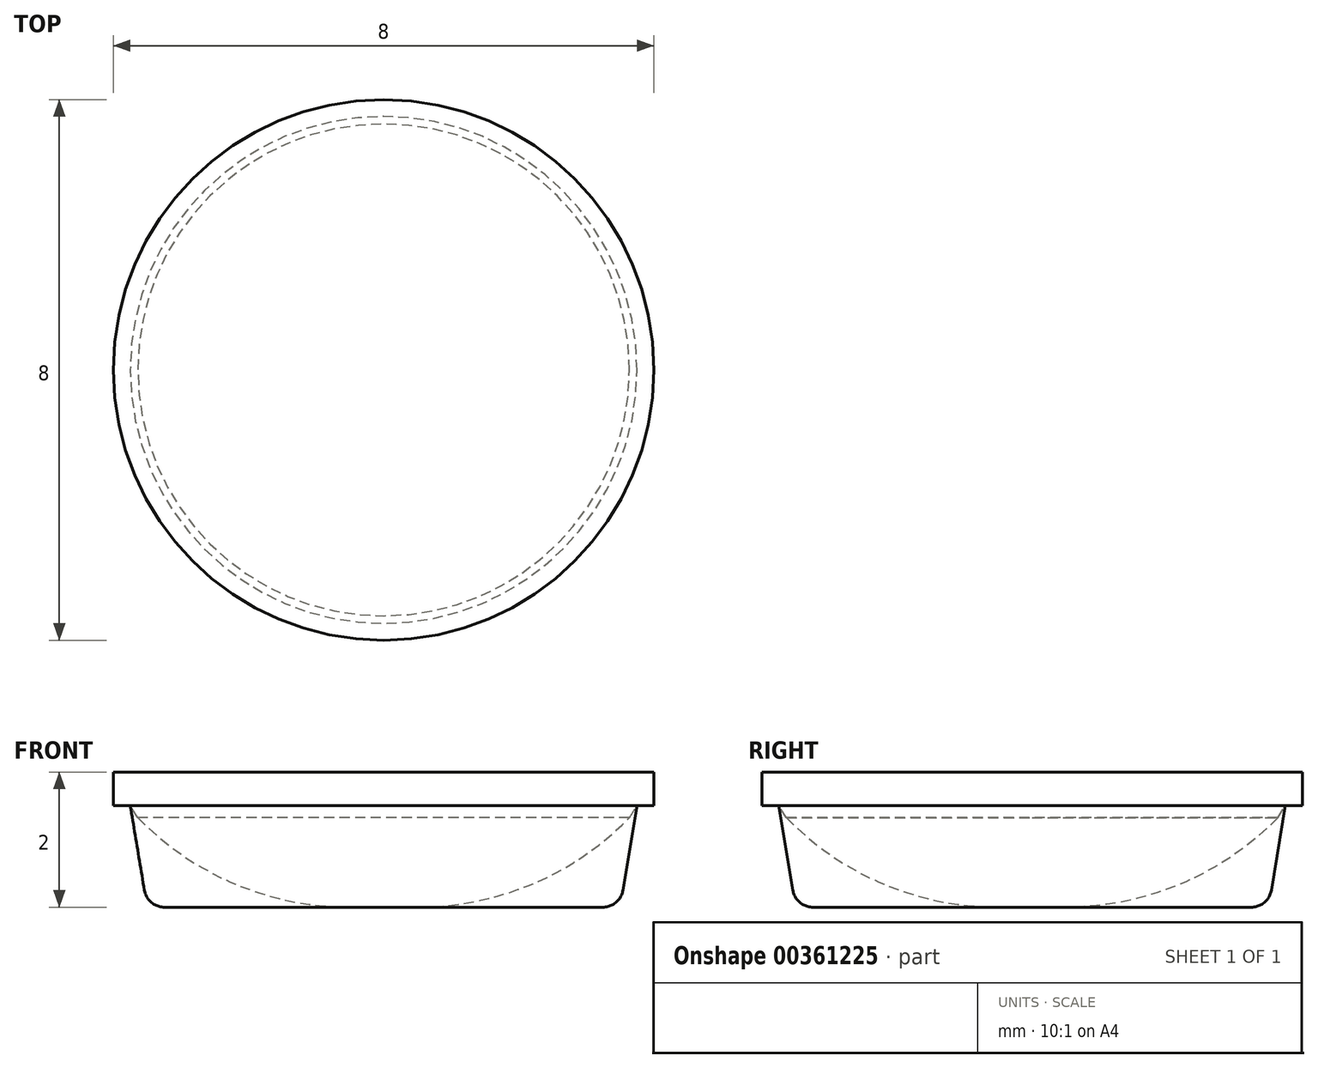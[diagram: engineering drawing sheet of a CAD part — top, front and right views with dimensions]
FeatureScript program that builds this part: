
annotation { "Feature Type Name" : "Feature", "Feature Type Description" : "" }
export const myFeature = defineFeature(function(context is Context, id is Id, definition is map)
    precondition{}
    {
        {
            var Q0;
            Q0=qCreatedBy(makeId("Front.planeOp"),FACE);
            var sketch = newSketch(context, id + "F0", { "sketchPlane" : qUnion([Q0])});
            skLineSegment(sketch, "E0", {"start": v(0, 0) * mm, "end": v(4, 0) * mm});
            skLineSegment(sketch, "E1", {"start": v(4, 0) * mm, "end": v(4, -0.5) * mm});
            skLineSegment(sketch, "E2", {"start": v(4, -0.5) * mm, "end": v(3.75, -0.5) * mm});
            skLineSegment(sketch, "E3", {"start": v(3.75, -0.5) * mm, "end": v(3.54, -1.75) * mm});
            skLineSegment(sketch, "E4", {"start": v(3.25, -2) * mm, "end": v(0, -2) * mm});
            skLineSegment(sketch, "E5", {"start": v(0, -2) * mm, "end": v(0, 0) * mm});
            skPoint(sketch, "E6.visualSharp", {"position": v(3.5, -2) * mm});
            skArc(sketch, "E6.filletArc", {"start": v(3.25, -2) * mm, "mid": v(3.44, -1.93) * mm, "end": v(3.54, -1.75) * mm});
            skSolve(sketch);
        }
        {
            var Q0;
            Q0=qSketchRegion(id+"F0",true);
            var Q1;
            Q1=sQuery(id+"F0.wireOp",EDGE,"E5");
            revolve(context, id + "F1", {"entities" : qUnion([Q0]), "axis" : qUnion([Q1]), "revolveType" : RevolveType.FULL});
        }
        {
            var Q0;
            Q0=qCreatedBy(makeId("Front.planeOp"),FACE);
            var sketch = newSketch(context, id + "F2", { "sketchPlane" : qUnion([Q0])});
            skLineSegment(sketch, "E7", {"start": v(0, 0) * mm, "end": v(4, 0) * mm});
            skLineSegment(sketch, "E8", {"start": v(4, 0) * mm, "end": v(4, -0.5) * mm});
            skLineSegment(sketch, "E9", {"start": v(4, -0.5) * mm, "end": v(3.75, -0.5) * mm});
            skLineSegment(sketch, "E10", {"start": v(3.75, -0.5) * mm, "end": v(3.64, -0.68) * mm});
            skLineSegment(sketch, "E11", {"start": v(0, 0) * mm, "end": v(0, -2) * mm});
            skLineSegment(sketch, "E12", {"start": v(0, -2) * mm, "end": v(0.5, -2) * mm});
            skArc(sketch, "E13", {"start": v(0.5, -2) * mm, "mid": v(2.2, -1.66) * mm, "end": v(3.64, -0.68) * mm});
            skSolve(sketch);
        }
        {
            var Q0;
            Q0=qSketchRegion(id+"F2",true);
            var Q1;
            Q1=sQuery(id+"F2.wireOp",EDGE,"E11");
            revolve(context, id + "F3", {"entities" : qUnion([Q0]), "axis" : qUnion([Q1]), "revolveType" : RevolveType.FULL});
        }
    });
